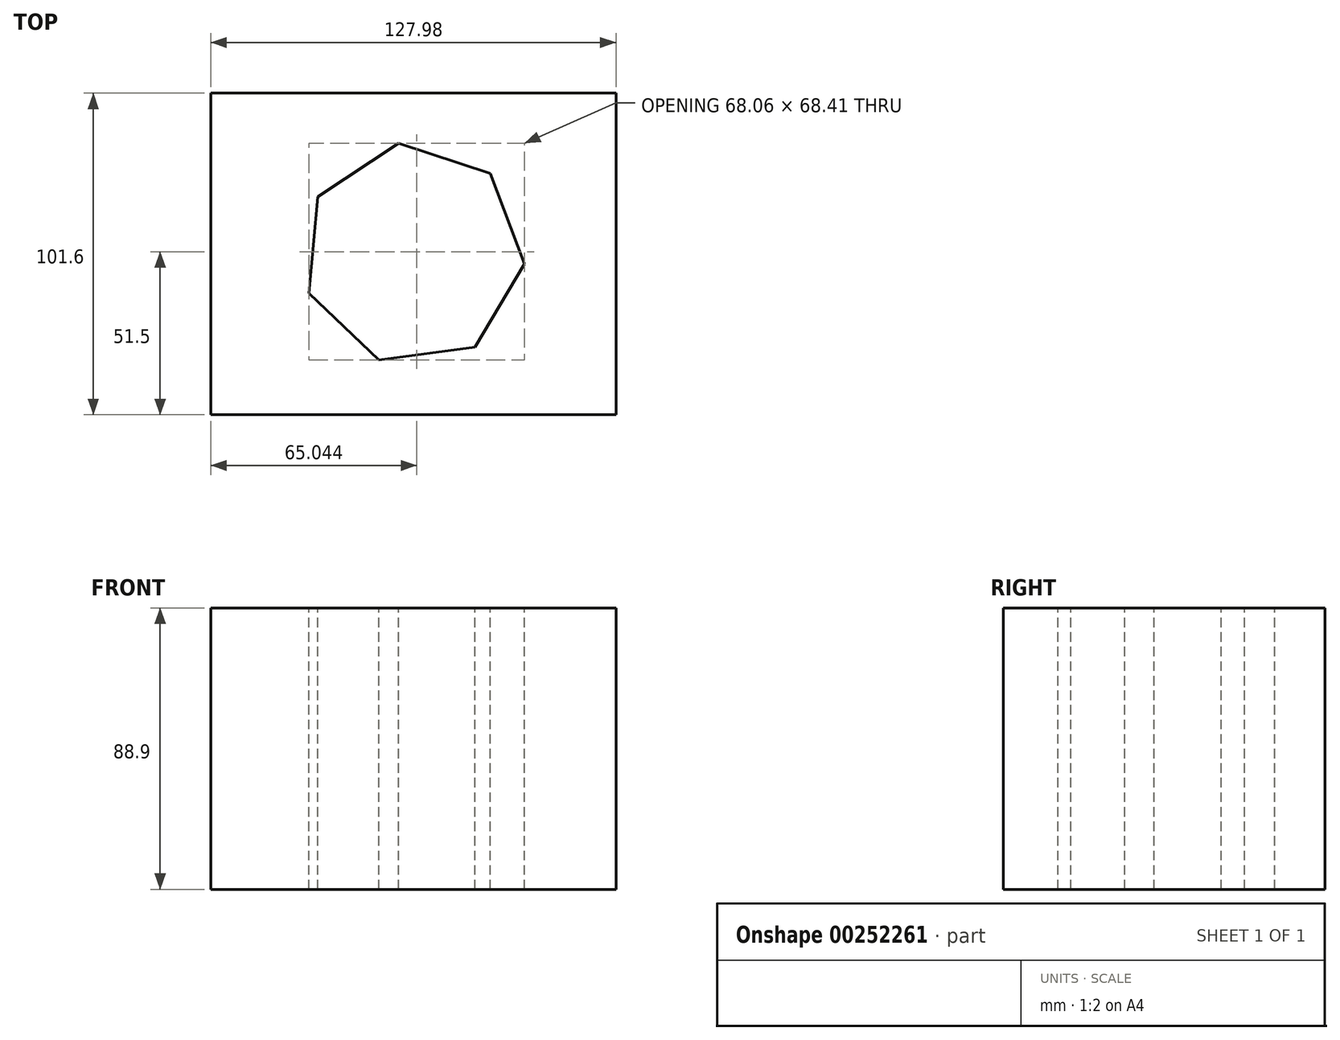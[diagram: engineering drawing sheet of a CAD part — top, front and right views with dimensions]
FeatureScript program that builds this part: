
annotation { "Feature Type Name" : "Feature", "Feature Type Description" : "" }
export const myFeature = defineFeature(function(context is Context, id is Id, definition is map)
    precondition{}
    {
        {
            var Q0;
            Q0=qCreatedBy(makeId("Front.planeOp"),FACE);
            var sketch = newSketch(context, id + "F0", { "sketchPlane" : qUnion([Q0])});
            skLineSegment(sketch, "E0.bottom", {"start": v(63.99, 44.45) * mm, "end": v(-63.99, 44.45) * mm});
            skLineSegment(sketch, "E0.top", {"start": v(63.99, -44.45) * mm, "end": v(-63.99, -44.45) * mm});
            skLineSegment(sketch, "E0.left", {"start": v(63.99, 44.45) * mm, "end": v(63.99, -44.45) * mm});
            skLineSegment(sketch, "E0.right", {"start": v(-63.99, 44.45) * mm, "end": v(-63.99, -44.45) * mm});
            skPoint(sketch, "E0.middle", {"position": v(0, 0) * mm});
            skSolve(sketch);
        }
        {
            var Q0;
            Q0 = qSketchRegion(id + "F0", true);
            extrude(context, id + "F1", {"entities" : qUnion([Q0]), "endBound" : BoundingType.SYMMETRIC, "depth" : 101.6 * mm});
        }
        {
            var Q0;
            Q0=qCreatedBy(makeId("Top.planeOp"),FACE);
            var sketch = newSketch(context, id + "F2", { "sketchPlane" : qUnion([Q0])});
            skCircle(sketch, "E1.cCircle", {"center": v(0, 0) * mm, "radius": 31.74 * mm, "construction": true});
            skLineSegment(sketch, "E1.0", {"start": v(24.33, 25.47) * mm, "end": v(35.08, -3.15) * mm});
            skLineSegment(sketch, "E1.1", {"start": v(35.08, -3.15) * mm, "end": v(19.41, -29.4) * mm});
            skLineSegment(sketch, "E1.2", {"start": v(19.41, -29.4) * mm, "end": v(-10.87, -33.5) * mm});
            skLineSegment(sketch, "E1.3", {"start": v(-10.87, -33.5) * mm, "end": v(-32.97, -12.39) * mm});
            skLineSegment(sketch, "E1.4", {"start": v(-32.97, -12.39) * mm, "end": v(-30.24, 18.06) * mm});
            skLineSegment(sketch, "E1.5", {"start": v(-30.24, 18.06) * mm, "end": v(-4.74, 34.9) * mm});
            skLineSegment(sketch, "E1.6", {"start": v(-4.74, 34.9) * mm, "end": v(24.33, 25.47) * mm});
            skPoint(sketch, "E1.0.midPoint", {"position": v(29.7, 11.16) * mm});
            skSolve(sketch);
        }
        {
            var Q0;
            Q0 = qSketchRegion(id + "F2", true);
            extrude(context, id + "F3", {"entities" : qUnion([Q0]), "operationType" : NewBodyOperationType.REMOVE, "endBound" : BoundingType.SYMMETRIC, "oppositeDirection" : true, "depth" : 127 * mm});
        }
    });
